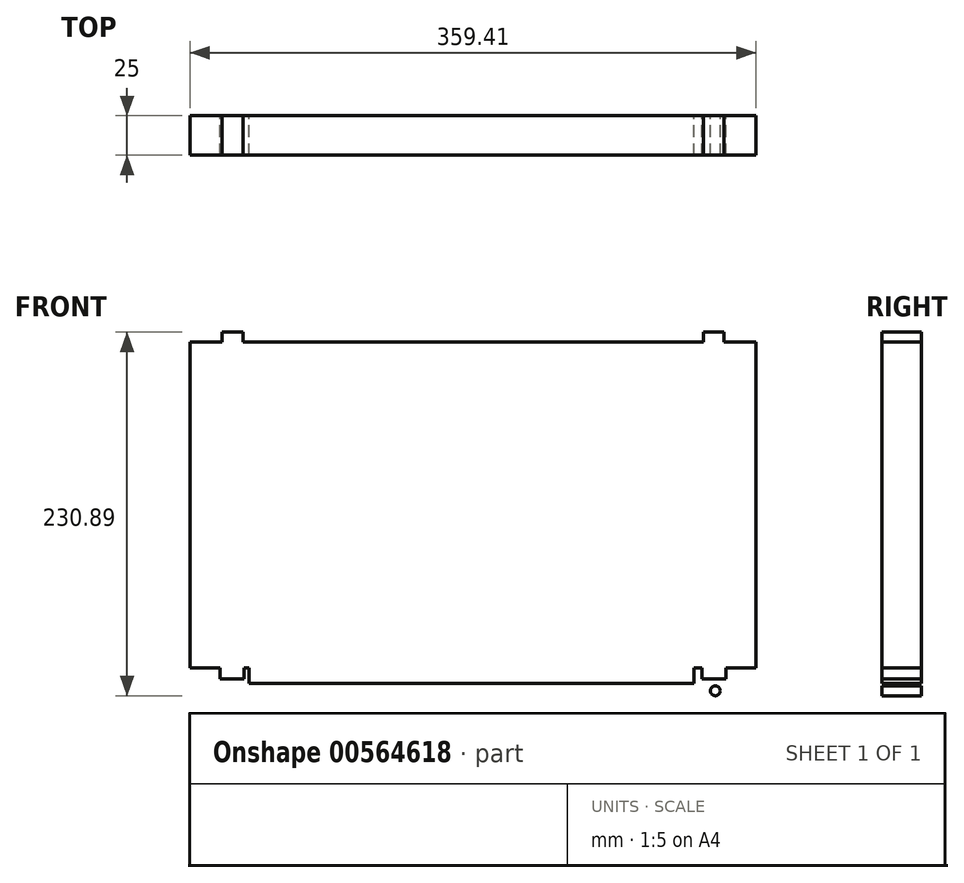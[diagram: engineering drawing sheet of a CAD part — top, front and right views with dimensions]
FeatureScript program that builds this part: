
annotation { "Feature Type Name" : "Feature", "Feature Type Description" : "" }
export const myFeature = defineFeature(function(context is Context, id is Id, definition is map)
    precondition{}
    {
        {
            var Q0;
            Q0=qCreatedBy(makeId("Front.planeOp"),FACE);
            var sketch = newSketch(context, id + "F0", { "sketchPlane" : qUnion([Q0])});
            skLineSegment(sketch, "E0.bottom", {"start": v(-180.8, 26.26) * mm, "end": v(178.62, 26.26) * mm});
            skLineSegment(sketch, "E0.top", {"start": v(-180.8, -180.75) * mm, "end": v(178.62, -180.75) * mm});
            skLineSegment(sketch, "E0.left", {"start": v(-180.8, 26.26) * mm, "end": v(-180.8, -180.75) * mm});
            skLineSegment(sketch, "E0.right", {"start": v(178.62, 26.26) * mm, "end": v(178.62, -180.75) * mm});
            skLineSegment(sketch, "E1", {"start": v(178.62, 26.26) * mm, "end": v(178.62, 32.36) * mm, "construction": true});
            skLineSegment(sketch, "E2", {"start": v(178.62, 32.36) * mm, "end": v(158.3, 32.36) * mm, "construction": true});
            skLineSegment(sketch, "E3", {"start": v(158.3, 32.36) * mm, "end": v(158.3, 26.26) * mm});
            skLineSegment(sketch, "E4", {"start": v(158.3, 32.36) * mm, "end": v(145.09, 32.36) * mm});
            skLineSegment(sketch, "E5", {"start": v(145.09, 32.36) * mm, "end": v(145.09, 26.26) * mm});
            skLineSegment(sketch, "E6", {"start": v(178.62, -180.75) * mm, "end": v(178.62, -187.99) * mm, "construction": true});
            skLineSegment(sketch, "E7", {"start": v(178.62, -187.99) * mm, "end": v(159.52, -187.99) * mm, "construction": true});
            skLineSegment(sketch, "E8", {"start": v(159.52, -187.99) * mm, "end": v(159.52, -180.75) * mm});
            skLineSegment(sketch, "E9", {"start": v(159.52, -187.99) * mm, "end": v(144.4, -187.99) * mm});
            skLineSegment(sketch, "E10", {"start": v(144.4, -187.99) * mm, "end": v(144.4, -180.75) * mm});
            skLineSegment(sketch, "E11", {"start": v(144.4, -187.99) * mm, "end": v(139.07, -187.99) * mm, "construction": true});
            skLineSegment(sketch, "E12", {"start": v(139.07, -180.75) * mm, "end": v(139.07, -190.79) * mm});
            skLineSegment(sketch, "E13", {"start": v(-1.09, 26.26) * mm, "end": v(-1.09, -180.75) * mm, "construction": true});
            skLineSegment(sketch, "E14.MirrorCS", {"start": v(-161.7, -187.99) * mm, "end": v(-146.58, -187.99) * mm});
            skLineSegment(sketch, "E15.MirrorCS", {"start": v(-180.8, -180.75) * mm, "end": v(-180.8, -187.99) * mm, "construction": true});
            skLineSegment(sketch, "E16.MirrorCS", {"start": v(-146.58, -187.99) * mm, "end": v(-143.25, -187.99) * mm, "construction": true});
            skLineSegment(sketch, "E17.MirrorCS", {"start": v(-161.7, -187.99) * mm, "end": v(-161.7, -180.75) * mm});
            skLineSegment(sketch, "E18.MirrorCS", {"start": v(-146.58, -187.99) * mm, "end": v(-146.58, -180.75) * mm});
            skLineSegment(sketch, "E19.MirrorCS", {"start": v(-143.25, -180.75) * mm, "end": v(-143.25, -190.79) * mm});
            skLineSegment(sketch, "E20.MirrorCS", {"start": v(-180.8, -187.99) * mm, "end": v(-161.7, -187.99) * mm, "construction": true});
            skLineSegment(sketch, "E21.MirrorCS", {"start": v(178.62, -180.75) * mm, "end": v(-180.8, -180.75) * mm});
            skLineSegment(sketch, "E22", {"start": v(-143.25, -190.79) * mm, "end": v(139.07, -190.79) * mm});
            skLineSegment(sketch, "E23.MirrorCS", {"start": v(-180.8, 26.26) * mm, "end": v(-180.8, 32.36) * mm, "construction": true});
            skLineSegment(sketch, "E24.MirrorCS", {"start": v(-147.27, 32.36) * mm, "end": v(-147.27, 26.26) * mm});
            skLineSegment(sketch, "E25.MirrorCS", {"start": v(-160.47, 32.36) * mm, "end": v(-160.47, 26.26) * mm});
            skLineSegment(sketch, "E26.MirrorCS", {"start": v(-160.47, 32.36) * mm, "end": v(-147.27, 32.36) * mm});
            skLineSegment(sketch, "E27.MirrorCS", {"start": v(-180.8, 32.36) * mm, "end": v(-160.47, 32.36) * mm, "construction": true});
            skLineSegment(sketch, "E28", {"start": v(152.78, -187.99) * mm, "end": v(152.78, -192.3) * mm});
            skCircle(sketch, "E29", {"center": v(152.78, -195.42) * mm, "radius": 3.11 * mm});
            skLineSegment(sketch, "E30", {"start": v(152.78, -195.42) * mm, "end": v(152.78, -192.3) * mm});
            skLineSegment(sketch, "E31", {"start": v(159.52, -187.99) * mm, "end": v(159.52, -195.42) * mm, "construction": true});
            skLineSegment(sketch, "E32", {"start": v(159.52, -195.42) * mm, "end": v(152.78, -195.42) * mm, "construction": true});
            skSolve(sketch);
        }
        {
            var Q0;
            Q0 = qSketchRegion(id + "F0", true);
            extrude(context, id + "F1", {"entities" : qUnion([Q0]), "depth" : 25 * mm, "offsetDistance" : 25 * mm});
        }
    });
